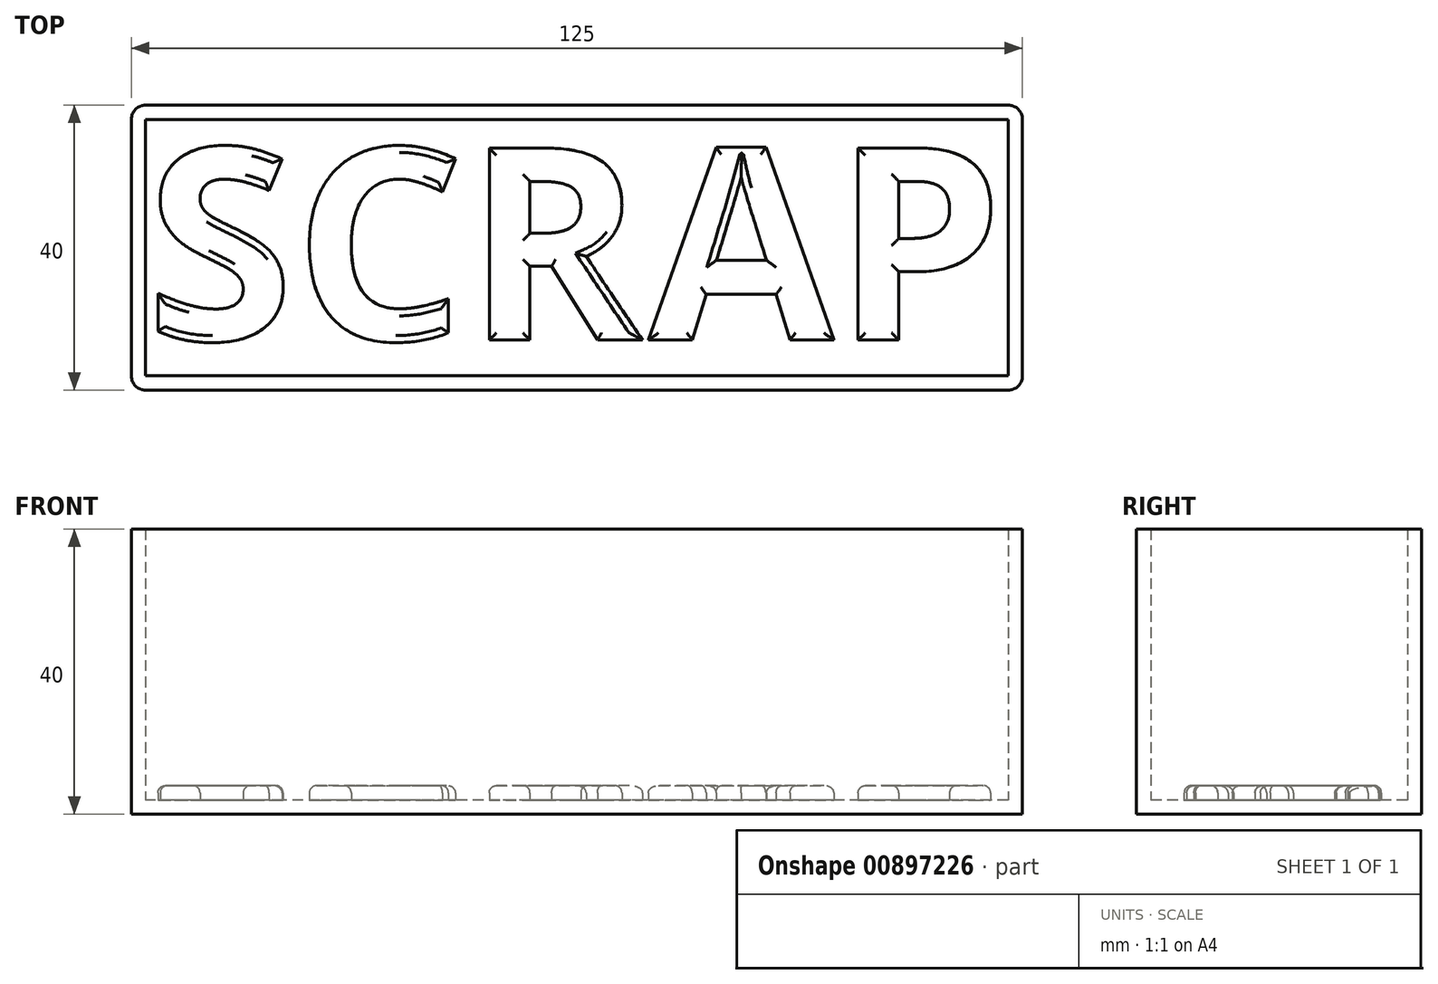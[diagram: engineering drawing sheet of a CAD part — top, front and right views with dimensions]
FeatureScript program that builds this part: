
annotation { "Feature Type Name" : "Feature", "Feature Type Description" : "" }
export const myFeature = defineFeature(function(context is Context, id is Id, definition is map)
    precondition{}
    {
        {
            var Q0;
            Q0=qCreatedBy(makeId("Top.planeOp"),FACE);
            var sketch = newSketch(context, id + "F0", { "sketchPlane" : qUnion([Q0])});
            skLineSegment(sketch, "E0.bottom", {"start": v(62.5, 20) * mm, "end": v(-62.5, 20) * mm});
            skLineSegment(sketch, "E0.top", {"start": v(62.5, -20) * mm, "end": v(-62.5, -20) * mm});
            skLineSegment(sketch, "E0.left", {"start": v(62.5, 20) * mm, "end": v(62.5, -20) * mm});
            skLineSegment(sketch, "E0.right", {"start": v(-62.5, 20) * mm, "end": v(-62.5, -20) * mm});
            skPoint(sketch, "E0.middle", {"position": v(0, 0) * mm});
            skSolve(sketch);
        }
        {
            var Q0;
            Q0 = qSketchRegion(id + "F0", true);
            extrude(context, id + "F1", {"entities" : qUnion([Q0]), "depth" : 40 * mm, "offsetDistance" : 25 * mm});
        }
        {
            var Q0;
            Q0=makeQuery(id+"F1.opExtrude","CAP_FACE",FACE,{"disambiguationData":[OSD([sQuery(id+"F0.wireOp",EDGE,"E0.bottom"),sQuery(id+"F0.wireOp",EDGE,"E0.top"),sQuery(id+"F0.wireOp",EDGE,"E0.left"),sQuery(id+"F0.wireOp",EDGE,"E0.right")])],"isStart":false});
            shell(context, id + "F2", {"entities" : qUnion([Q0]), "thickness" : 2 * mm});
        }
        {
            var Q0;
            Q0=makeQuery(id+"F1.opExtrude","SWEPT_EDGE",EDGE,{"disambiguationData":[OSD([sQuery(id+"F0.wireOp",EDGE,"E0.bottom"),sQuery(id+"F0.wireOp",EDGE,"E0.left")])]});
            var Q1;
            Q1=makeQuery(id+"F1.opExtrude","SWEPT_EDGE",EDGE,{"disambiguationData":[OSD([sQuery(id+"F0.wireOp",EDGE,"E0.bottom"),sQuery(id+"F0.wireOp",EDGE,"E0.right")])]});
            var Q2;
            Q2=makeQuery(id+"F1.opExtrude","SWEPT_EDGE",EDGE,{"disambiguationData":[OSD([sQuery(id+"F0.wireOp",EDGE,"E0.top"),sQuery(id+"F0.wireOp",EDGE,"E0.right")])]});
            var Q3;
            Q3=makeQuery(id+"F1.opExtrude","SWEPT_EDGE",EDGE,{"disambiguationData":[OSD([sQuery(id+"F0.wireOp",EDGE,"E0.top"),sQuery(id+"F0.wireOp",EDGE,"E0.left")])]});
            fillet(context, id + "F3", {"entities" : qUnion([Q0, Q1, Q2, Q3]), "radius" : 2 * mm, "tangentPropagation" : true, "allowEdgeOverflow" : false});
        }
        {
            var Q0;
            Q0=makeQuery(id+"F2.opShell","OFFSET_FACE",FACE,{"disambiguationData":[OSD([sQuery(id+"F0.wireOp",EDGE,"E0.bottom"),sQuery(id+"F0.wireOp",EDGE,"E0.top"),sQuery(id+"F0.wireOp",EDGE,"E0.left"),sQuery(id+"F0.wireOp",EDGE,"E0.right")])]});
            var sketch = newSketch(context, id + "F4", { "sketchPlane" : qUnion([Q0])});
            skText(sketch, "E1", { "text": "SCRAP", "fontName": "OpenSans-Bold.ttf"});
            const initialGuessF4  = {"E1": [-0.0605, -0.01296, 1, 0, 0.02716]};
            skSetInitialGuess(sketch, initialGuessF4);
            skSolve(sketch);
        }
        {
            var Q0;
            Q0 = qSketchRegion(id + "F4", true);
            extrude(context, id + "F5", {"entities" : qUnion([Q0]), "operationType" : NewBodyOperationType.ADD, "depth" : 2 * mm, "offsetDistance" : 25 * mm});
        }
        {
            var Q0;
            Q0=makeQuery(id+"F5.opExtrude","CAP_FACE",FACE,{"disambiguationData":[OSD([sQuery(id+"F4.wireOp",EDGE,"E1.sketch_text.stroke-0"),sQuery(id+"F4.wireOp",EDGE,"E1.sketch_text.stroke-1"),sQuery(id+"F4.wireOp",EDGE,"E1.sketch_text.stroke-2"),sQuery(id+"F4.wireOp",EDGE,"E1.sketch_text.stroke-3"),sQuery(id+"F4.wireOp",EDGE,"E1.sketch_text.stroke-4"),sQuery(id+"F4.wireOp",EDGE,"E1.sketch_text.stroke-5"),sQuery(id+"F4.wireOp",EDGE,"E1.sketch_text.stroke-6"),sQuery(id+"F4.wireOp",EDGE,"E1.sketch_text.stroke-7"),sQuery(id+"F4.wireOp",EDGE,"E1.sketch_text.stroke-8"),sQuery(id+"F4.wireOp",EDGE,"E1.sketch_text.stroke-9"),sQuery(id+"F4.wireOp",EDGE,"E1.sketch_text.stroke-10"),sQuery(id+"F4.wireOp",EDGE,"E1.sketch_text.stroke-11"),sQuery(id+"F4.wireOp",EDGE,"E1.sketch_text.stroke-12"),sQuery(id+"F4.wireOp",EDGE,"E1.sketch_text.stroke-13"),sQuery(id+"F4.wireOp",EDGE,"E1.sketch_text.stroke-14"),sQuery(id+"F4.wireOp",EDGE,"E1.sketch_text.stroke-15"),sQuery(id+"F4.wireOp",EDGE,"E1.sketch_text.stroke-16"),sQuery(id+"F4.wireOp",EDGE,"E1.sketch_text.stroke-17"),sQuery(id+"F4.wireOp",EDGE,"E1.sketch_text.stroke-18"),sQuery(id+"F4.wireOp",EDGE,"E1.sketch_text.stroke-19"),sQuery(id+"F4.wireOp",EDGE,"E1.sketch_text.stroke-20"),sQuery(id+"F4.wireOp",EDGE,"E1.sketch_text.stroke-21"),sQuery(id+"F4.wireOp",EDGE,"E1.sketch_text.stroke-22"),sQuery(id+"F4.wireOp",EDGE,"E1.sketch_text.stroke-23"),sQuery(id+"F4.wireOp",EDGE,"E1.sketch_text.stroke-24"),sQuery(id+"F4.wireOp",EDGE,"E1.sketch_text.stroke-25"),sQuery(id+"F4.wireOp",EDGE,"E1.sketch_text.stroke-26"),sQuery(id+"F4.wireOp",EDGE,"E1.sketch_text.stroke-27")])],"isStart":false});
            var Q1;
            Q1=makeQuery(id+"F5.opExtrude","CAP_FACE",FACE,{"disambiguationData":[OSD([sQuery(id+"F4.wireOp",EDGE,"E1.sketch_text.stroke-28"),sQuery(id+"F4.wireOp",EDGE,"E1.sketch_text.stroke-29"),sQuery(id+"F4.wireOp",EDGE,"E1.sketch_text.stroke-30"),sQuery(id+"F4.wireOp",EDGE,"E1.sketch_text.stroke-31"),sQuery(id+"F4.wireOp",EDGE,"E1.sketch_text.stroke-32"),sQuery(id+"F4.wireOp",EDGE,"E1.sketch_text.stroke-33"),sQuery(id+"F4.wireOp",EDGE,"E1.sketch_text.stroke-34"),sQuery(id+"F4.wireOp",EDGE,"E1.sketch_text.stroke-35"),sQuery(id+"F4.wireOp",EDGE,"E1.sketch_text.stroke-36"),sQuery(id+"F4.wireOp",EDGE,"E1.sketch_text.stroke-37"),sQuery(id+"F4.wireOp",EDGE,"E1.sketch_text.stroke-38"),sQuery(id+"F4.wireOp",EDGE,"E1.sketch_text.stroke-39"),sQuery(id+"F4.wireOp",EDGE,"E1.sketch_text.stroke-40"),sQuery(id+"F4.wireOp",EDGE,"E1.sketch_text.stroke-41"),sQuery(id+"F4.wireOp",EDGE,"E1.sketch_text.stroke-42")])],"isStart":false});
            var Q2;
            Q2=makeQuery(id+"F5.opExtrude","CAP_FACE",FACE,{"disambiguationData":[OSD([sQuery(id+"F4.wireOp",EDGE,"E1.sketch_text.stroke-43"),sQuery(id+"F4.wireOp",EDGE,"E1.sketch_text.stroke-44"),sQuery(id+"F4.wireOp",EDGE,"E1.sketch_text.stroke-45"),sQuery(id+"F4.wireOp",EDGE,"E1.sketch_text.stroke-46"),sQuery(id+"F4.wireOp",EDGE,"E1.sketch_text.stroke-47"),sQuery(id+"F4.wireOp",EDGE,"E1.sketch_text.stroke-48"),sQuery(id+"F4.wireOp",EDGE,"E1.sketch_text.stroke-49"),sQuery(id+"F4.wireOp",EDGE,"E1.sketch_text.stroke-50"),sQuery(id+"F4.wireOp",EDGE,"E1.sketch_text.stroke-51"),sQuery(id+"F4.wireOp",EDGE,"E1.sketch_text.stroke-52"),sQuery(id+"F4.wireOp",EDGE,"E1.sketch_text.stroke-53"),sQuery(id+"F4.wireOp",EDGE,"E1.sketch_text.stroke-54"),sQuery(id+"F4.wireOp",EDGE,"E1.sketch_text.stroke-55"),sQuery(id+"F4.wireOp",EDGE,"E1.sketch_text.stroke-56"),sQuery(id+"F4.wireOp",EDGE,"E1.sketch_text.stroke-57"),sQuery(id+"F4.wireOp",EDGE,"E1.sketch_text.stroke-58"),sQuery(id+"F4.wireOp",EDGE,"E1.sketch_text.stroke-59"),sQuery(id+"F4.wireOp",EDGE,"E1.sketch_text.stroke-60"),sQuery(id+"F4.wireOp",EDGE,"E1.sketch_text.stroke-61")])],"isStart":false});
            var Q3;
            Q3=makeQuery(id+"F5.opExtrude","CAP_FACE",FACE,{"disambiguationData":[OSD([sQuery(id+"F4.wireOp",EDGE,"E1.sketch_text.stroke-62"),sQuery(id+"F4.wireOp",EDGE,"E1.sketch_text.stroke-63"),sQuery(id+"F4.wireOp",EDGE,"E1.sketch_text.stroke-64"),sQuery(id+"F4.wireOp",EDGE,"E1.sketch_text.stroke-65"),sQuery(id+"F4.wireOp",EDGE,"E1.sketch_text.stroke-66"),sQuery(id+"F4.wireOp",EDGE,"E1.sketch_text.stroke-67"),sQuery(id+"F4.wireOp",EDGE,"E1.sketch_text.stroke-68"),sQuery(id+"F4.wireOp",EDGE,"E1.sketch_text.stroke-69"),sQuery(id+"F4.wireOp",EDGE,"E1.sketch_text.stroke-70"),sQuery(id+"F4.wireOp",EDGE,"E1.sketch_text.stroke-71"),sQuery(id+"F4.wireOp",EDGE,"E1.sketch_text.stroke-72"),sQuery(id+"F4.wireOp",EDGE,"E1.sketch_text.stroke-73")])],"isStart":false});
            var Q4;
            Q4=makeQuery(id+"F5.opExtrude","CAP_FACE",FACE,{"disambiguationData":[OSD([sQuery(id+"F4.wireOp",EDGE,"E1.sketch_text.stroke-74"),sQuery(id+"F4.wireOp",EDGE,"E1.sketch_text.stroke-75"),sQuery(id+"F4.wireOp",EDGE,"E1.sketch_text.stroke-76"),sQuery(id+"F4.wireOp",EDGE,"E1.sketch_text.stroke-77"),sQuery(id+"F4.wireOp",EDGE,"E1.sketch_text.stroke-78"),sQuery(id+"F4.wireOp",EDGE,"E1.sketch_text.stroke-79"),sQuery(id+"F4.wireOp",EDGE,"E1.sketch_text.stroke-80"),sQuery(id+"F4.wireOp",EDGE,"E1.sketch_text.stroke-81"),sQuery(id+"F4.wireOp",EDGE,"E1.sketch_text.stroke-82"),sQuery(id+"F4.wireOp",EDGE,"E1.sketch_text.stroke-83"),sQuery(id+"F4.wireOp",EDGE,"E1.sketch_text.stroke-84"),sQuery(id+"F4.wireOp",EDGE,"E1.sketch_text.stroke-85"),sQuery(id+"F4.wireOp",EDGE,"E1.sketch_text.stroke-86"),sQuery(id+"F4.wireOp",EDGE,"E1.sketch_text.stroke-87"),sQuery(id+"F4.wireOp",EDGE,"E1.sketch_text.stroke-88"),sQuery(id+"F4.wireOp",EDGE,"E1.sketch_text.stroke-89")])],"isStart":false});
            fillet(context, id + "F6", {"entities" : qUnion([Q0, Q1, Q2, Q3, Q4]), "radius" : 1 * mm, "tangentPropagation" : true, "allowEdgeOverflow" : false});
        }
    });
